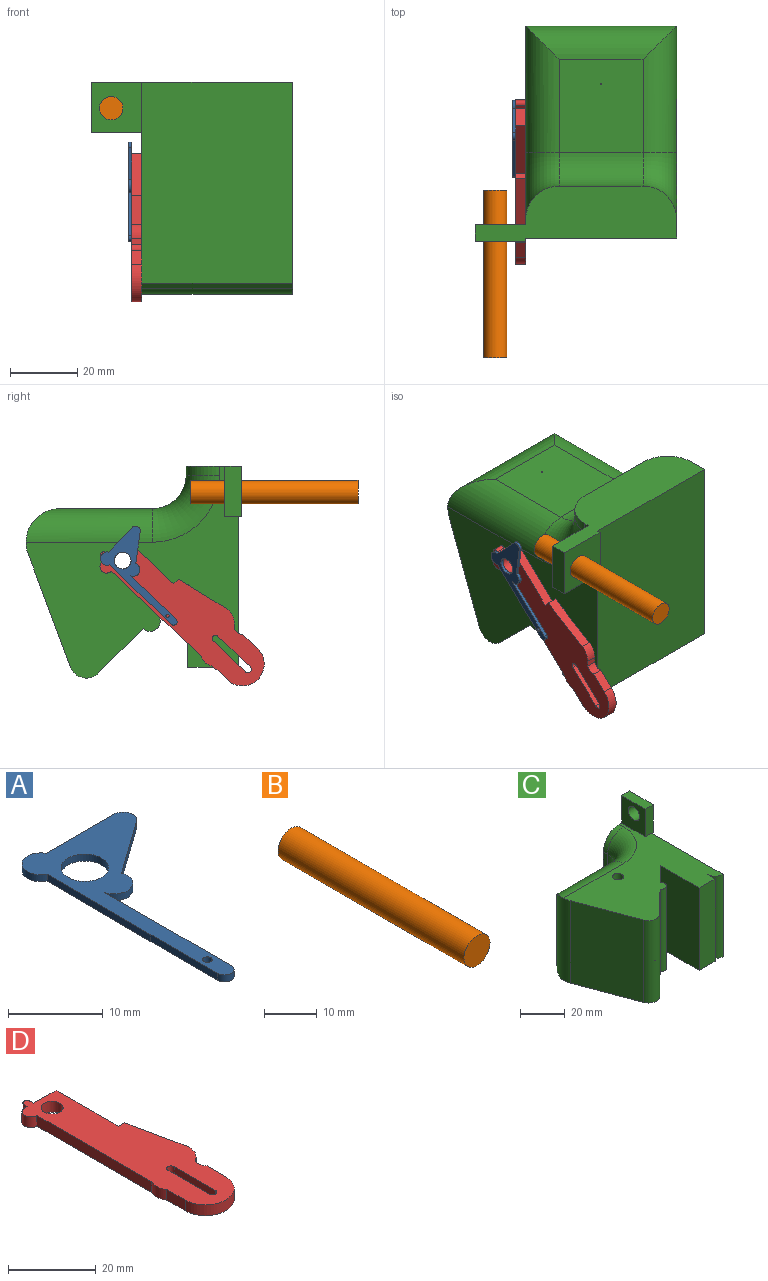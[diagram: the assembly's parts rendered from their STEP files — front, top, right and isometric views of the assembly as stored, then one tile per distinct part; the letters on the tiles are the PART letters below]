
ASSEMBLY  parts=4 mates=3
PART A: 13 faces, bbox 15.3x30.4x0.9 mm
  f0: plane 10x0.9mm, normal (-1,0,0), area 9mm2, adj f1,f10,f11,f12
  f1: cylinder r=1mm len=2mm, axis (0,0,-1), area 2.8mm2, adj f0,f2,f11,f12
  f2: plane 18.94x0.9mm, normal (1,0,0), area 17mm2, adj f1,f3,f11,f12
  f3: cylinder r=2mm len=3.93mm, axis (0,0,-1), area 5.8mm2, adj f2,f4,f11,f12
  f4: plane 7.84x5.6mm, normal (0.58,-0.81,0), area 8.7mm2, adj f3,f5,f11,f12
  f5: cylinder r=1.43mm len=2.6mm, axis (0,0,-1), area 3.2mm2, adj f4,f6,f11,f12
  f6: plane 10.09x0.9mm, normal (0,1,0), area 9.1mm2, adj f5,f7,f11,f12
  f7: cylinder r=2mm len=3.8mm, axis (0,0,-1), area 6.8mm2, adj f6,f10,f11,f12
  f8: cylinder r=0.5mm len=1mm, axis (0,0,-1), area 2.8mm2, adj f11,f12
  f9: cylinder r=2.5mm len=5mm, axis (0,0,-1), area 14.1mm2, adj f11,f12
  f10: plane 15.62x0.9mm, normal (-1,0.01,0), area 14.1mm2, adj f0,f7,f11,f12
  f11: plane 30.42x15.27mm, normal (0,0,1), area 125.4mm2, adj f0,f1,f2,f3,f4,f5,f6,f7
  f12: plane 30.42x15.27mm, normal (0,0,-1), area 125.4mm2, adj f0,f1,f2,f3,f4,f5,f6,f7
PART B: 3 faces, bbox 7x50x7 mm
  f0: cylinder r=3.5mm len=50mm, axis (0,1,0), area 1099.6mm2, adj f1,f2
  f1: plane 7x7mm, normal (0,-1,0), area 38.5mm2, adj f0
  f2: plane 7x7mm, normal (0,1,0), area 38.5mm2, adj f0
PART C: 31 faces, bbox 67.1x63.2x60 mm
  f0: plane 60x45mm, normal (1,0,0), area 2700mm2, adj f1,f12,f14,f15,f24
  f1: plane 60x16.52mm, normal (0,1,0), area 730.3mm2, adj f0,f2,f14,f15,f17,f23,f24,f25
  f2: plane 25x2.7mm, normal (-1,0,0), area 67.5mm2, adj f1,f17,f21,f23
  f3: plane 27.79x25mm, normal (0,1,0), area 694.6mm2, adj f16,f18,f20,f21,f30
  f4: plane 45x33.79mm, normal (-0.94,-0.35,0), area 1623.9mm2, adj f5,f14,f15,f18
  f5: cylinder r=5.01mm len=45mm, axis (0,0,-1), area 458.8mm2, adj f4,f6,f14,f15,f30
  f6: plane 45x13.36mm, normal (0.7,-0.71,0), area 841.7mm2, adj f5,f7,f14,f15
  f7: cylinder r=3mm len=45mm, axis (0,0,-1), area 406.5mm2, adj f6,f8,f14,f15
  f8: plane 45x9.08mm, normal (0.7,-0.71,0), area 572.3mm2, adj f7,f9,f14,f15
  f9: plane 45x24.54mm, normal (-1,0,0), area 1104.5mm2, adj f8,f10,f14,f15
  f10: plane 45x10mm, normal (0,-1,0), area 450mm2, adj f9,f11,f14,f15
  f11: plane 45x5mm, normal (1,0,0), area 225mm2, adj f10,f12,f14,f15
  f12: cylinder r=5mm len=45mm, axis (0,0,-1), area 353.4mm2, adj f0,f11,f14,f15
  f13: cylinder r=2.5mm len=45mm, axis (0,0,-1), area 706.9mm2, adj f14,f15
  f14: plane 63.3x63.25mm, normal (0,0,1), area 1980.2mm2, adj f0,f1,f4,f5,f6,f7,f8,f9
  f15: plane 63.3x63.25mm, normal (0,0,-1), area 2040.2mm2, adj f0,f1,f4,f5,f6,f7,f8,f9
  f16: cylinder r=10mm len=37.79mm, axis (-1,0,0), area 536.5mm2, adj f3,f15,f18,f19
  f17: cylinder r=10mm len=10mm, axis (0,-1,0), area 42.4mm2, adj f1,f2,f15,f19
  f18: cylinder r=10mm len=45mm, axis (0,0,-1), area 754.1mm2, adj f3,f4,f14,f15,f16,f20
  f19: torus R=20mm, axis (0,0,1), area 336.4mm2, adj f15,f16,f17,f21
  f20: cylinder r=10mm len=37.79mm, axis (1,0,0), area 536.5mm2, adj f3,f14,f18,f22
  f21: cylinder r=10mm len=25mm, axis (0,0,-1), area 392.7mm2, adj f2,f3,f19,f22
  f22: torus R=20mm, axis (0,0,1), area 336.4mm2, adj f14,f20,f21,f23
  f23: cylinder r=10mm len=10mm, axis (0,1,0), area 42.4mm2, adj f1,f2,f14,f22
  f24: plane 15x1mm, normal (0,0,-1), area 15mm2, adj f0,f1,f26,f28
  f25: plane 15x15mm, normal (-1,0,0), area 186.5mm2, adj f1,f14,f27,f28,f29
  f26: plane 15x15mm, normal (1,0,0), area 186.5mm2, adj f1,f24,f27,f28,f29
  f27: plane 15x5mm, normal (0,0,1), area 75mm2, adj f1,f25,f26,f28
  f28: plane 15x5mm, normal (0,-1,0), area 75mm2, adj f14,f24,f25,f26,f27
  f29: cylinder r=3.5mm len=7mm, axis (1,0,0), area 110mm2, adj f25,f26
  f30: cylinder r=0.12mm len=50.52mm, axis (0,-1,0), area 39.7mm2, adj f3,f5
PART D: 24 faces, bbox 17.6x59.9x3 mm
  f0: cylinder r=6.5mm len=13mm, axis (0,0,-1), area 61.3mm2, adj f1,f21,f22,f23
  f1: plane 6x3mm, normal (1,0,0), area 18mm2, adj f0,f2,f22,f23
  f2: cylinder r=2.92mm len=3.04mm, axis (0,0,-1), area 9.8mm2, adj f1,f3,f22,f23
  f3: plane 3x1.3mm, normal (0.68,-0.74,0), area 5.3mm2, adj f2,f4,f22,f23
  f4: cylinder r=5mm len=4.71mm, axis (0,0,-1), area 15.5mm2, adj f3,f5,f22,f23
  f5: plane 16.37x3.45mm, normal (0.98,0.21,0), area 50.2mm2, adj f4,f6,f22,f23
  f6: plane 3x2mm, normal (0,1,0), area 6mm2, adj f5,f7,f22,f23
  f7: plane 20x3mm, normal (1,0,0), area 60mm2, adj f6,f8,f22,f23
  f8: plane 7.18x3mm, normal (0.01,1,0), area 21.5mm2, adj f7,f9,f22,f23
  f9: plane 3x1.01mm, normal (1,0,0), area 3mm2, adj f8,f10,f22,f23
  f10: cylinder r=1mm len=3mm, axis (0,0,-1), area 9.4mm2, adj f9,f11,f22,f23
  f11: plane 3x0.99mm, normal (-1,0,0), area 3mm2, adj f10,f12,f22,f23
  f12: plane 3x0.8mm, normal (0.01,1,0), area 2.4mm2, adj f11,f13,f22,f23
  f13: cylinder r=2mm len=4mm, axis (0,0,-1), area 18.8mm2, adj f12,f14,f22,f23
  f14: plane 37x3mm, normal (-1,0,0), area 111mm2, adj f13,f15,f22,f23
  f15: cylinder r=4mm len=4.45mm, axis (0,0,-1), area 14.2mm2, adj f14,f21,f22,f23
  f16: cylinder r=1mm len=3mm, axis (0,0,-1), area 9.5mm2, adj f17,f19,f22,f23
  f17: plane 13.35x3mm, normal (-1,0,0), area 40mm2, adj f16,f18,f22,f23
  f18: cylinder r=1mm len=3mm, axis (0,0,-1), area 9.5mm2, adj f17,f19,f22,f23
  f19: plane 13.35x3mm, normal (1,0,0), area 40mm2, adj f16,f18,f22,f23
  f20: cylinder r=2.5mm len=5mm, axis (0,0,-1), area 47.1mm2, adj f22,f23
  f21: plane 6x3mm, normal (-1,0,0), area 18mm2, adj f0,f15,f22,f23
  f22: plane 59.93x17.57mm, normal (0,0,1), area 658.8mm2, adj f0,f1,f2,f3,f4,f5,f6,f7
  f23: plane 59.93x17.57mm, normal (0,0,-1), area 658.8mm2, adj f0,f1,f2,f3,f4,f5,f6,f7
PLACE A rot(axis=(0.35,-0.87,-0.35),97.9deg) t=(158.9,41.34,-37.96)mm
PLACE B t=(152.8,36.36,0.71)mm
PLACE C rot(axis=(0.58,-0.58,-0.58),120deg) t=(206.9,46.14,-51.51)mm fixed
PLACE D rot(axis=(0.35,-0.87,-0.35),97.9deg) t=(161.9,20.86,-50.58)mm
MATE slider C.f29 <-> B.f0  axis (0,1,0) through (152.8,26.14,0.71)mm
MATE fastened A.f9 <-> D.f20  axis (1,0,0) through (158.9,56.59,-19.71)mm
MATE revolute D.f20 <-> C.f13  axis (1,0,0) through (161.9,56.59,-19.71)mm
